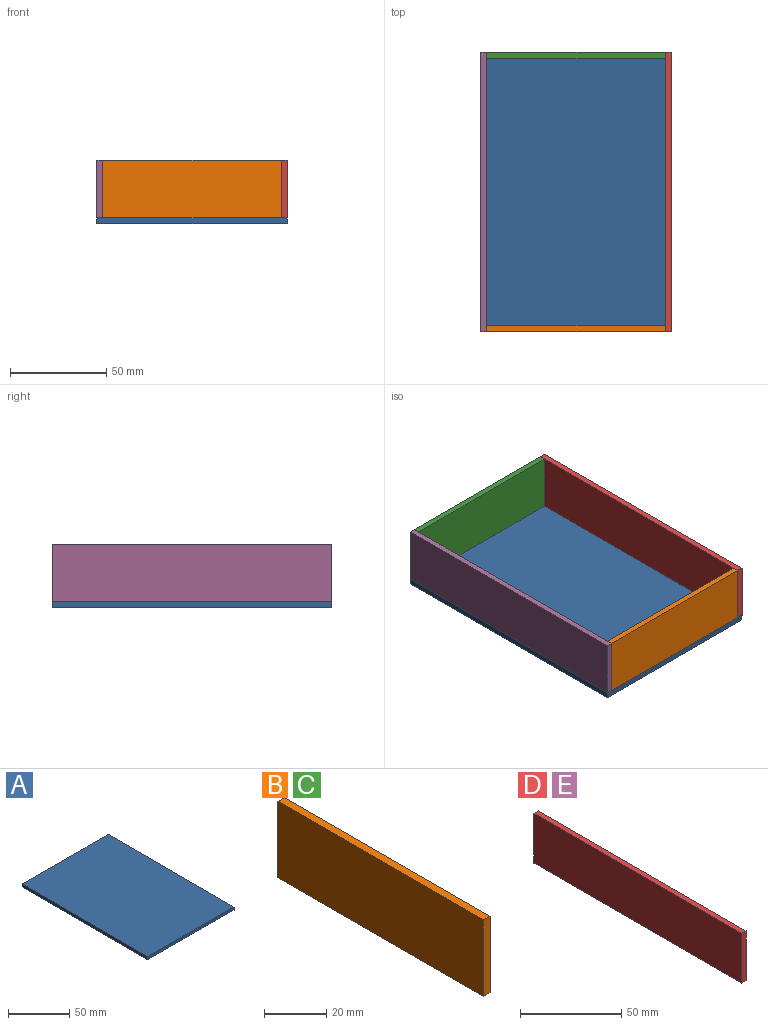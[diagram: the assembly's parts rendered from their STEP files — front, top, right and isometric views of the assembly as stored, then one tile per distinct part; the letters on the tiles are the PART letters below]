
ASSEMBLY  parts=5 mates=4
PART A: 6 faces, bbox 99x145x3 mm
  f0: plane 99x3mm, normal (0,1,0), area 297mm2, adj f1,f3,f4,f5
  f1: plane 145x3mm, normal (-1,0,0), area 435mm2, adj f0,f2,f4,f5
  f2: plane 99x3mm, normal (0,-1,0), area 297mm2, adj f1,f3,f4,f5
  f3: plane 145x3mm, normal (1,0,0), area 435mm2, adj f0,f2,f4,f5
  f4: plane 145x99mm, normal (0,0,1), area 14355mm2, adj f0,f1,f2,f3
  f5: plane 145x99mm, normal (0,0,-1), area 14355mm2, adj f0,f1,f2,f3
PART B: 6 faces, bbox 3x93x30 mm
  f0: plane 30x3mm, normal (0,1,0), area 90mm2, adj f1,f3,f4,f5
  f1: plane 93x30mm, normal (-1,0,0), area 2790mm2, adj f0,f2,f4,f5
  f2: plane 30x3mm, normal (0,-1,0), area 90mm2, adj f1,f3,f4,f5
  f3: plane 93x30mm, normal (1,0,0), area 2790mm2, adj f0,f2,f4,f5
  f4: plane 93x3mm, normal (0,0,1), area 279mm2, adj f0,f1,f2,f3
  f5: plane 93x3mm, normal (0,0,-1), area 279mm2, adj f0,f1,f2,f3
PART C: same geometry as B
PART D: 6 faces, bbox 3x145x30 mm
  f0: plane 30x3mm, normal (0,1,0), area 90mm2, adj f1,f3,f4,f5
  f1: plane 145x30mm, normal (-1,0,0), area 4350mm2, adj f0,f2,f4,f5
  f2: plane 30x3mm, normal (0,-1,0), area 90mm2, adj f1,f3,f4,f5
  f3: plane 145x30mm, normal (1,0,0), area 4350mm2, adj f0,f2,f4,f5
  f4: plane 145x3mm, normal (0,0,1), area 435mm2, adj f0,f1,f2,f3
  f5: plane 145x3mm, normal (0,0,-1), area 435mm2, adj f0,f1,f2,f3
PART E: same geometry as D
PLACE A t=(-5.89,-11.49,0.8)mm
PLACE B rot(axis=(0,0,-1),90deg) t=(-35.22,-34.02,3.8)mm
PLACE C rot(axis=(0,0,-1),90deg) t=(-35.22,107.98,3.8)mm
PLACE D t=(64.23,-25.51,3.8)mm
PLACE E t=(-31.77,-25.51,3.8)mm
MATE fastened D.f5 <-> A.f4  axis (0,0,-1) through (46.57,-72.66,3.8)mm
MATE fastened B.f0 <-> D.f1  axis (1,0,0) through (43.57,-72.66,3.8)mm
MATE fastened C.f0 <-> D.f1  axis (1,0,0) through (43.57,72.34,3.8)mm
MATE fastened E.f5 <-> A.f4  axis (0,0,-1) through (-52.43,-72.66,3.8)mm
